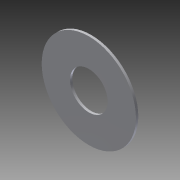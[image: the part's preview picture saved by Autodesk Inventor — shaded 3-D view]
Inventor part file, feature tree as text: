
AUTODESK INVENTOR PART (.ipt)
format: ipt  version: 2013 (Build 170138000, 138)  size: 76,288 bytes
history: native  units: mm
features: other x1, extrude x1, sketch x1
ambient origin geometry x8: Origin, YZ Plane, XZ Plane, XY Plane, X Axis, Y Axis, Z Axis, Center Point
feature tree (3):
  other  "ソリッド1"
  extrude  "押し出し1"  Depth=20.0mm
  sketch  "スケッチ1"
